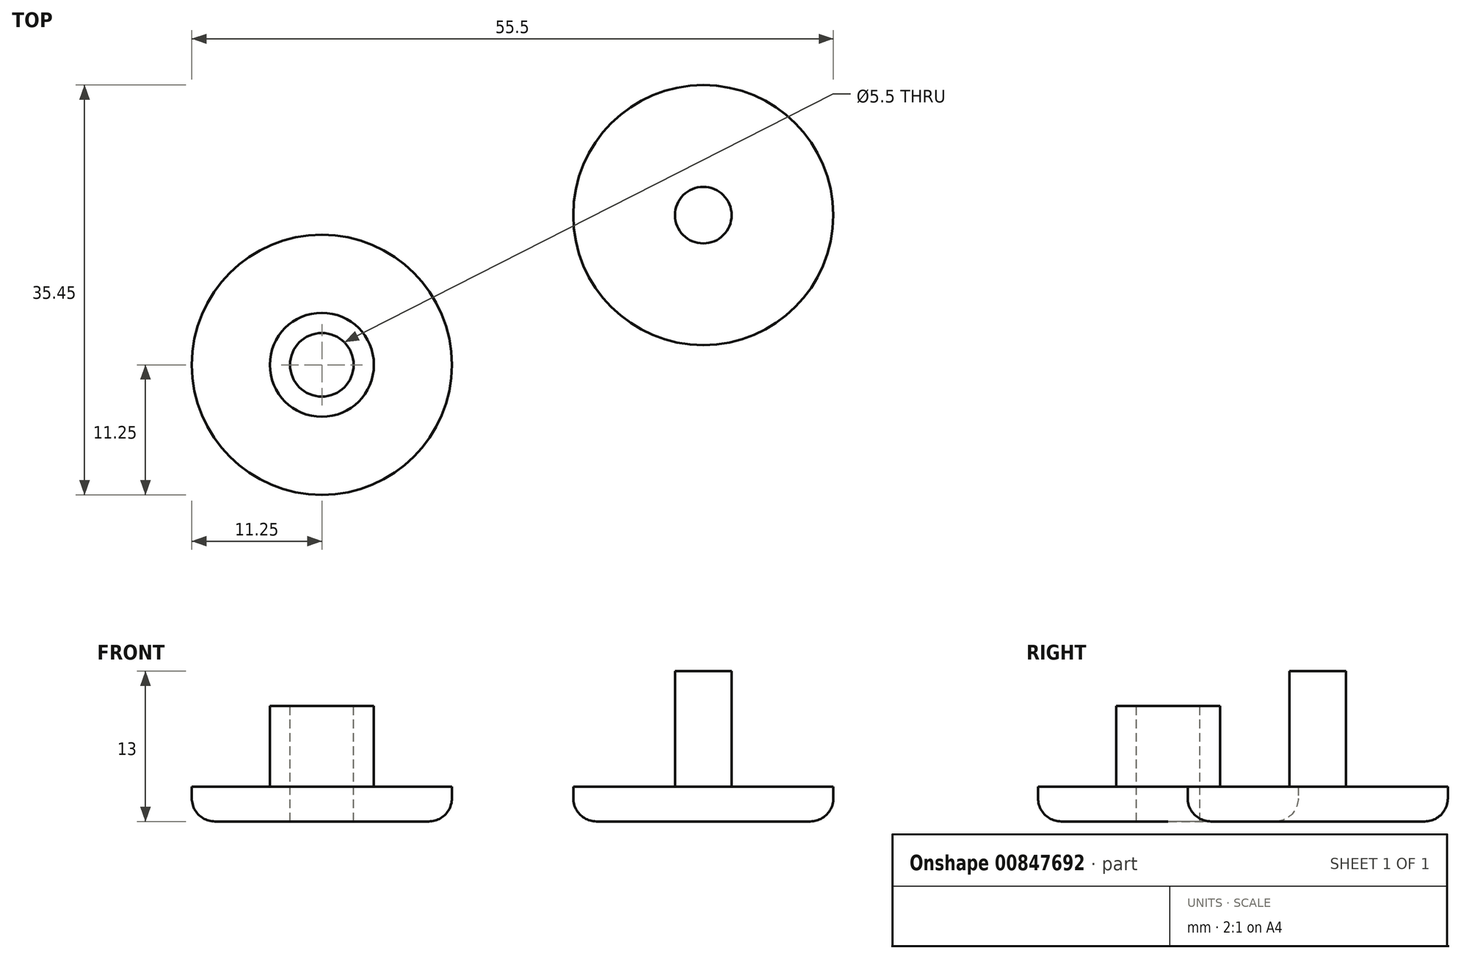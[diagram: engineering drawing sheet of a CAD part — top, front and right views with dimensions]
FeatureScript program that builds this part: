
annotation { "Feature Type Name" : "Feature", "Feature Type Description" : "" }
export const myFeature = defineFeature(function(context is Context, id is Id, definition is map)
    precondition{}
    {
        {
            var Q0;
            Q0=qCreatedBy(makeId("Top.planeOp"),FACE);
            var sketch = newSketch(context, id + "F0", { "sketchPlane" : qUnion([Q0])});
            skCircle(sketch, "E0", {"center": v(0, 0) * mm, "radius": 11.25 * mm});
            skSolve(sketch);
        }
        {
            var Q0;
            Q0=makeQuery(id+"F0.imprint","IMPRINT",FACE,{"disambiguationData":[TD([[makeQuery(id+"F0.imprint","IMPRINT",EDGE,{"derivedFrom":sQuery(id+"F0.wireOp",EDGE,"E0")}),1.0]])]});
            extrude(context, id + "F1", {"entities" : qUnion([Q0]), "depth" : 3 * mm, "offsetDistance" : 25 * mm});
        }
        {
            var Q0;
            Q0=makeQuery(id+"F1.opExtrude","CAP_FACE",FACE,{"disambiguationData":[OSD([sQuery(id+"F0.wireOp",EDGE,"E0")])],"isStart":false});
            var sketch = newSketch(context, id + "F2", { "sketchPlane" : qUnion([Q0])});
            skCircle(sketch, "E1", {"center": v(0, 0) * mm, "radius": 4.5 * mm});
            skSolve(sketch);
        }
        {
            var Q0;
            Q0=makeQuery(id+"F2.imprint","IMPRINT",FACE,{"disambiguationData":[TD([[makeQuery(id+"F2.imprint","IMPRINT",EDGE,{"derivedFrom":sQuery(id+"F2.wireOp",EDGE,"E1")}),1.0]])]});
            extrude(context, id + "F3", {"entities" : qUnion([Q0]), "operationType" : NewBodyOperationType.ADD, "depth" : 7 * mm, "offsetDistance" : 25 * mm});
        }
        {
            var Q0;
            Q0=makeQuery(id+"F3.opExtrude","CAP_FACE",FACE,{"disambiguationData":[OSD([sQuery(id+"F2.wireOp",EDGE,"E1")])],"isStart":false});
            var sketch = newSketch(context, id + "F4", { "sketchPlane" : qUnion([Q0])});
            skCircle(sketch, "E2", {"center": v(0, 0) * mm, "radius": 2.75 * mm});
            skSolve(sketch);
        }
        {
            var Q0;
            Q0=makeQuery(id+"F4.imprint","IMPRINT",FACE,{"disambiguationData":[TD([[makeQuery(id+"F4.imprint","IMPRINT",EDGE,{"derivedFrom":sQuery(id+"F4.wireOp",EDGE,"E2")}),1.0]])]});
            extrude(context, id + "F5", {"entities" : qUnion([Q0]), "operationType" : NewBodyOperationType.REMOVE, "oppositeDirection" : true, "depth" : 70.6 * mm, "offsetDistance" : 25 * mm});
        }
        {
            var Q0;
            Q0=qCreatedBy(makeId("Top.planeOp"),FACE);
            var sketch = newSketch(context, id + "F6", { "sketchPlane" : qUnion([Q0])});
            skCircle(sketch, "E3", {"center": v(33, 12.95) * mm, "radius": 11.25 * mm});
            skSolve(sketch);
        }
        {
            var Q0;
            Q0=makeQuery(id+"F6.imprint","IMPRINT",FACE,{"disambiguationData":[TD([[makeQuery(id+"F6.imprint","IMPRINT",EDGE,{"derivedFrom":sQuery(id+"F6.wireOp",EDGE,"E3")}),1.0]])]});
            extrude(context, id + "F7", {"entities" : qUnion([Q0]), "depth" : 3 * mm, "offsetDistance" : 25 * mm});
        }
        {
            var Q0;
            Q0=makeQuery(id+"F7.opExtrude","CAP_FACE",FACE,{"disambiguationData":[OSD([sQuery(id+"F6.wireOp",EDGE,"E3")])],"isStart":false});
            var sketch = newSketch(context, id + "F8", { "sketchPlane" : qUnion([Q0])});
            skCircle(sketch, "E4", {"center": v(33, 12.95) * mm, "radius": 2.45 * mm});
            skSolve(sketch);
        }
        {
            var Q0;
            Q0=makeQuery(id+"F8.imprint","IMPRINT",FACE,{"disambiguationData":[TD([[makeQuery(id+"F8.imprint","IMPRINT",EDGE,{"derivedFrom":sQuery(id+"F8.wireOp",EDGE,"E4")}),1.0]])]});
            extrude(context, id + "F9", {"entities" : qUnion([Q0]), "operationType" : NewBodyOperationType.ADD, "depth" : 10 * mm, "offsetDistance" : 25 * mm});
        }
        {
            var Q0;
            Q0=makeQuery(id+"F7.opExtrude","CAP_EDGE",EDGE,{"disambiguationData":[OSD([sQuery(id+"F6.wireOp",EDGE,"E3")])],"isStart":true});
            var Q1;
            Q1=makeQuery(id+"F1.opExtrude","CAP_EDGE",EDGE,{"disambiguationData":[OSD([sQuery(id+"F0.wireOp",EDGE,"E0")])],"isStart":true});
            fillet(context, id + "F10", {"entities" : qUnion([Q0, Q1]), "radius" : 2 * mm, "tangentPropagation" : true, "allowEdgeOverflow" : false});
        }
    });
